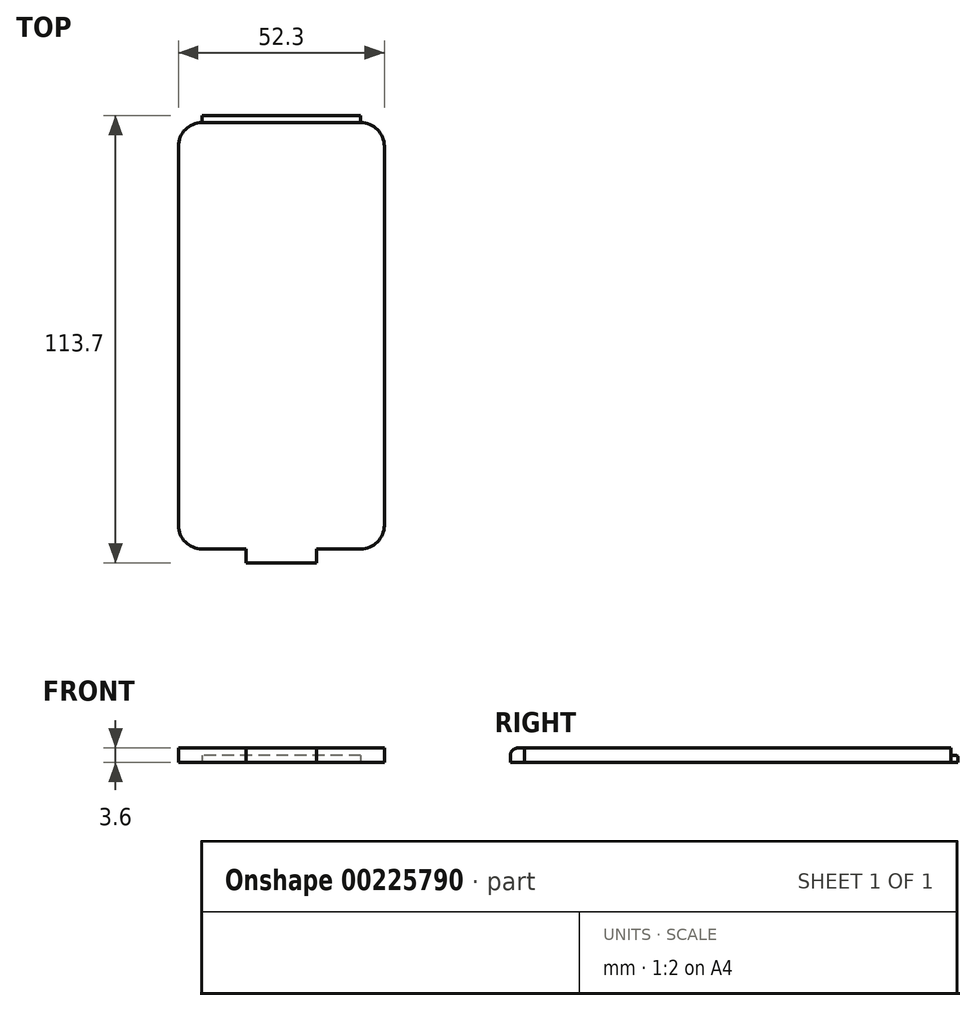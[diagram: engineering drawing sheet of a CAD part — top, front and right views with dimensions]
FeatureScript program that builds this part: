
annotation { "Feature Type Name" : "Feature", "Feature Type Description" : "" }
export const myFeature = defineFeature(function(context is Context, id is Id, definition is map)
    precondition{}
    {
        {
            assignVariable(context, id + "F0", {"name" : "O", "anyValue" : 3.6});
        }
        {
            var Q0;
            Q0=qCreatedBy(makeId("Top.planeOp"),FACE);
            var sketch = newSketch(context, id + "F1", { "sketchPlane" : qUnion([Q0])});
            skLineSegment(sketch, "E0.bottom", {"start": v(20.15, -54.15) * mm, "end": v(-20.15, -54.15) * mm});
            skLineSegment(sketch, "E0.top", {"start": v(20.15, 54.15) * mm, "end": v(-20.15, 54.15) * mm});
            skLineSegment(sketch, "E0.left", {"start": v(26.15, -48.15) * mm, "end": v(26.15, 48.15) * mm});
            skLineSegment(sketch, "E0.right", {"start": v(-26.15, -48.15) * mm, "end": v(-26.15, 48.15) * mm});
            skPoint(sketch, "E0.middle", {"position": v(0, 0) * mm});
            skPoint(sketch, "E1.visualSharp", {"position": v(26.15, 54.15) * mm});
            skArc(sketch, "E1.filletArc", {"start": v(26.15, 48.15) * mm, "mid": v(24.4, 52.4) * mm, "end": v(20.15, 54.15) * mm});
            skPoint(sketch, "E2.visualSharp", {"position": v(-26.15, 54.15) * mm});
            skArc(sketch, "E2.filletArc", {"start": v(-20.15, 54.15) * mm, "mid": v(-24.4, 52.4) * mm, "end": v(-26.15, 48.15) * mm});
            skPoint(sketch, "E3.visualSharp", {"position": v(-26.15, -54.15) * mm});
            skArc(sketch, "E3.filletArc", {"start": v(-26.15, -48.15) * mm, "mid": v(-24.4, -52.4) * mm, "end": v(-20.15, -54.15) * mm});
            skPoint(sketch, "E4.visualSharp", {"position": v(26.15, -54.15) * mm});
            skArc(sketch, "E4.filletArc", {"start": v(20.15, -54.15) * mm, "mid": v(24.4, -52.4) * mm, "end": v(26.15, -48.15) * mm});
            skSolve(sketch);
        }
        {
            var Q0;
            Q0=makeQuery(id+"F1.imprint","IMPRINT",FACE,{"disambiguationData":[TD([[makeQuery(id+"F1.imprint","IMPRINT",EDGE,{"derivedFrom":sQuery(id+"F1.wireOp",EDGE,"E0.bottom")}),-1.0]])]});
            extrude(context, id + "F2", {"entities" : qUnion([Q0]), "depth" : (getVariable(context, 'O')) * mm});
        }
        {
            var Q0;
            Q0=makeQuery(id+"F2.opExtrude","SWEPT_FACE",FACE,{"disambiguationData":[OSD([sQuery(id+"F1.wireOp",EDGE,"E0.bottom")])]});
            var sketch = newSketch(context, id + "F3", { "sketchPlane" : qUnion([Q0])});
            skLineSegment(sketch, "E5.bottom", {"start": v(-9, 3.6) * mm, "end": v(9, 3.6) * mm});
            skLineSegment(sketch, "E5.top", {"start": v(-9, 0) * mm, "end": v(9, 0) * mm});
            skLineSegment(sketch, "E5.left", {"start": v(-9, 3.6) * mm, "end": v(-9, 0) * mm});
            skLineSegment(sketch, "E5.right", {"start": v(9, 3.6) * mm, "end": v(9, 0) * mm});
            skLineSegment(sketch, "E6", {"start": v(-20.15, 1.8) * mm, "end": v(-9, 1.8) * mm});
            skLineSegment(sketch, "E7", {"start": v(9, 1.8) * mm, "end": v(20.15, 1.8) * mm});
            skSolve(sketch);
        }
        {
            var Q0;
            Q0=makeQuery(id+"F3.imprint","IMPRINT",FACE,{"disambiguationData":[TD([[makeQuery(id+"F3.imprint","IMPRINT",EDGE,{"derivedFrom":sQuery(id+"F3.wireOp",EDGE,"E5.bottom")}),1.0]])]});
            extrude(context, id + "F4", {"entities" : qUnion([Q0]), "operationType" : NewBodyOperationType.ADD, "depth" : 3.6 * mm});
        }
        {
            var Q0;
            Q0=makeQuery(id+"F2.opExtrude","SWEPT_FACE",FACE,{"disambiguationData":[OSD([sQuery(id+"F1.wireOp",EDGE,"E0.top")])]});
            var sketch = newSketch(context, id + "F5", { "sketchPlane" : qUnion([Q0])});
            skLineSegment(sketch, "E8", {"start": v(-20.15, 1.8) * mm, "end": v(20.15, 1.8) * mm});
            skSolve(sketch);
        }
        {
            var Q0;
            {var subQ0=sQuery(id+"F5.wireOp",EDGE,"E8");Q0=makeQuery(id+"F5.imprint","IMPRINT",FACE,{"disambiguationData":[TD([[makeQuery(id+"F5.imprint","IMPRINT",EDGE,{"derivedFrom":subQ0}),-1.0]])]});}
            extrude(context, id + "F6", {"entities" : qUnion([Q0]), "operationType" : NewBodyOperationType.ADD, "depth" : (3.6 / 2) * mm});
        }
        {
            var Q0;
            Q0=makeQuery(id+"F4.opExtrude","CAP_EDGE",EDGE,{"disambiguationData":[OSD([sQuery(id+"F3.wireOp",EDGE,"E5.bottom")])],"isStart":false});
            fillet(context, id + "F7", {"entities" : qUnion([Q0]), "radius" : 1.9 * mm, "tangentPropagation" : true, "allowEdgeOverflow" : false});
        }
        {
            var Q0;
            Q0=makeQuery(id+"F6.opExtrude","CAP_EDGE",EDGE,{"disambiguationData":[OSD([sQuery(id+"F5.wireOp",EDGE,"E8")])],"isStart":false});
            fillet(context, id + "F8", {"entities" : qUnion([Q0]), "radius" : .5 * mm, "tangentPropagation" : true, "allowEdgeOverflow" : false});
        }
    });
